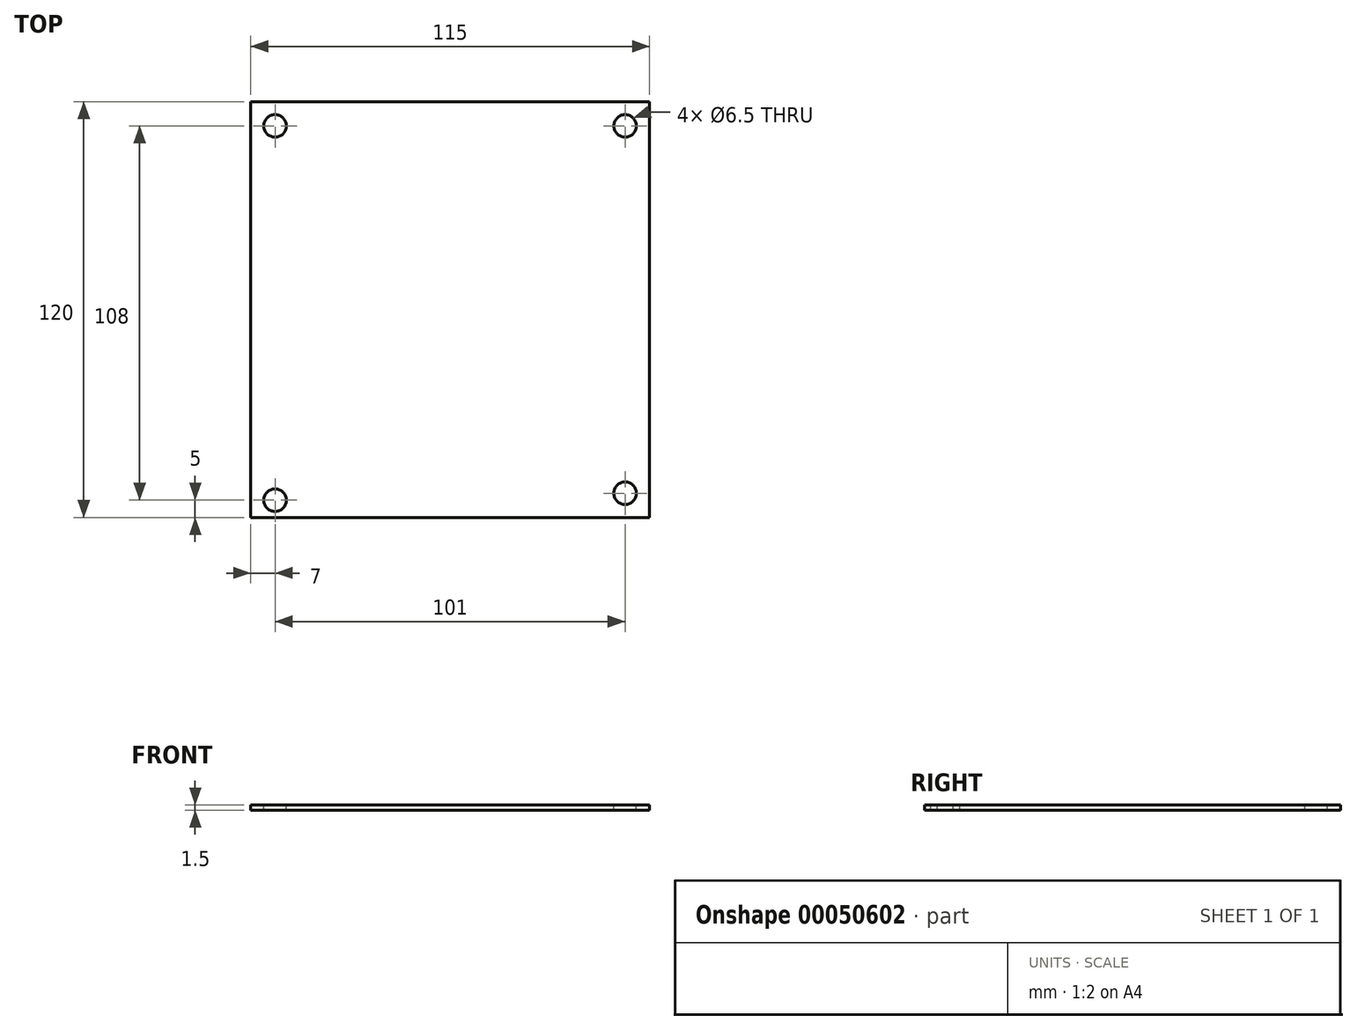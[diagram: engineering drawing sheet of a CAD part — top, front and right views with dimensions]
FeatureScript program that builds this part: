
annotation { "Feature Type Name" : "Feature", "Feature Type Description" : "" }
export const myFeature = defineFeature(function(context is Context, id is Id, definition is map)
    precondition{}
    {
        {
            var Q0;
            Q0=qCreatedBy(makeId("Top.planeOp"),FACE);
            var sketch = newSketch(context, id + "F0", { "sketchPlane" : qUnion([Q0])});
            skLineSegment(sketch, "E0.bottom", {"start": v(-52.5, 65) * mm, "end": v(62.5, 65) * mm});
            skLineSegment(sketch, "E0.top", {"start": v(-52.5, -55) * mm, "end": v(62.5, -55) * mm});
            skLineSegment(sketch, "E0.left", {"start": v(-52.5, 65) * mm, "end": v(-52.5, -55) * mm});
            skLineSegment(sketch, "E0.right", {"start": v(62.5, 65) * mm, "end": v(62.5, -55) * mm});
            skCircle(sketch, "E1", {"center": v(-45.5, 58) * mm, "radius": 3.25 * mm});
            skCircle(sketch, "E2", {"center": v(-45.5, 58) * mm, "radius": 1.6 * mm});
            skCircle(sketch, "E3", {"center": v(55.5, 58) * mm, "radius": 3.25 * mm});
            skCircle(sketch, "E4", {"center": v(55.5, 58) * mm, "radius": 1.6 * mm});
            skCircle(sketch, "E5", {"center": v(55.5, -48) * mm, "radius": 3.25 * mm});
            skCircle(sketch, "E6", {"center": v(55.5, -48) * mm, "radius": 1.6 * mm});
            skCircle(sketch, "E7", {"center": v(-45.5, -50) * mm, "radius": 3.25 * mm});
            skCircle(sketch, "E8", {"center": v(-45.5, -50) * mm, "radius": 1.6 * mm});
            skSolve(sketch);
        }
        {
            var Q0;
            Q0=makeQuery(id+"F0.imprint","IMPRINT",FACE,{"disambiguationData":[TD([[makeQuery(id+"F0.imprint","IMPRINT",EDGE,{"derivedFrom":sQuery(id+"F0.wireOp",EDGE,"E0.bottom")}),-1.0]])]});
            extrude(context, id + "F1", {"entities" : qUnion([Q0]), "oppositeDirection" : true, "depth" : 1.5 * mm});
        }
    });
